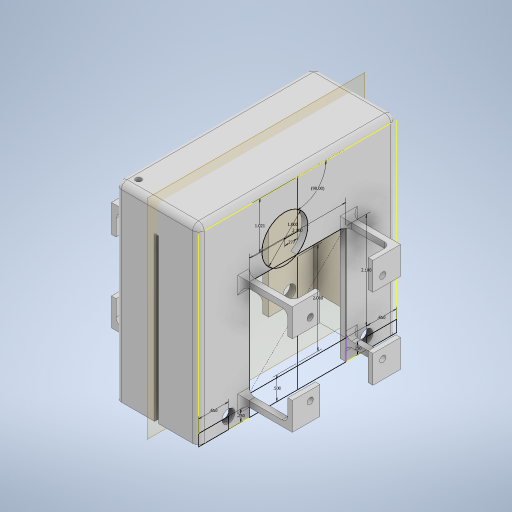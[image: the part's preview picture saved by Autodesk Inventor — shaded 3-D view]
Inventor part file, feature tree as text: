
AUTODESK INVENTOR PART (.ipt)
format: ipt  version: 2024.1 (Build 281209000, 209)  size: 548,352 bytes
history: native  units: in
note: dims shown in document units (in); Inventor stores cm internally (conversion verified against a paired STEP export)
features: sketch x9, extrude x8, hole x3, fillet x3, plane x1, mirror x1
ambient origin geometry x8: Origin, YZ Plane, XZ Plane, XY Plane, X Axis, Y Axis, Z Axis, Center Point
bodies: Solid1 (feature_tree)
feature tree (25):
  extrude  "Extrusion1"  Depth=4.0in
  sketch  "Sketch2"  dims[d2=0.25in d3=0.25in]
  extrude  "Extrusion2"  Depth=0.25in
  hole  "Hole1"  [1 undecoded]
  extrude  "Extrusion3"  Depth=4.3in
  fillet  "Fillet1"  Radius=4.0in
  extrude  "Extrusion4"  Depth=0.25in
  hole  "Hole2"  [1 undecoded]
  extrude  "Extrusion5"  Depth=2.1in
  extrude  "Extrusion6"  Depth=0.125in TaperAngle=0.0deg
  extrude  "Extrusion7"  Depth=0.125in
  extrude  "Extrusion8"  Depth=0.125in
  hole  "Hole3"  [1 undecoded]
  fillet  "Fillet2"  [1 undecoded]
  fillet  "Fillet3"  Radius=0.277in
  plane  "Work Plane1"
  mirror  "Mirror1"
  sketch  "Sketch1"  dims[d0=1.0in d1=4.0in]
  sketch  "Sketch3"  dims[d4=1.55in d5=4.05in]
  sketch  "Sketch4"  dims[d6=1.8in d7=4.3in d8=4.0in d9=0.0in]
  sketch  "Sketch5"  dims[d12=0.65in d13=0.25in]
  sketch  "Sketch6"  dims[d14=0.5in d15=2.0in]
  sketch  "Sketch7"  dims[d16=2.1in d17=2.1in]
  sketch  "Sketch8"  dims[d18=0.125in d19=0.0in]
  sketch  "Sketch9"  dims[d20=0.281in d21=0.75in d22=0.438in d23=0.25in d24=0.5635in d25=1.0in d26=0.8108in d27=0.125in d28=0.0in d29=0.125in d30=1.021in d31=90.0deg d33=0.0in d34=0.0in d37=0.277in d38=1.0in d39=0.125in d40=0.125in d41=0.125in d42=0.75in d43=0.375in d44=0.25in d45=0.5635in d46=1.0in d47=0.8108in d48=0.65in d49=0.25in d50=0.775in d51=0.325in d52=0.325in d53=0.25in d54=0.0in d55=0.5in d56=0.0312in d57=0.0312in d58=0.0825in d59=3.6in d60=0.25in d61=0.0in d62=0.0312in d63=0.0312in d64=0.0625in d65=3.6in d66=0.125in d67=0.125in d68=0.125in d69=0.125in d70=0.125in d71=0.125in d72=0.125in d73=0.125in d74=0.9646in d75=0.0in d76=0.6in d77=0.6in d78=1.5748in d79=1.5748in d80=0.6in d81=0.6in d82=0.6in d83=0.6in d84=0.6in d85=0.6in d86=0.1in d87=0.0in d88=1.5748in d89=1.5748in d90=0.136in d91=0.75in d92=0.375in d93=0.25in d94=0.5635in d95=1.0in d96=0.8108in d97=0.125in d98=0.125in]
note: 4 required parameter values undecoded (feature->parameter linkage not recoverable at this tier; creation-order binding heuristic only, values carry confidence <= 0.55)
